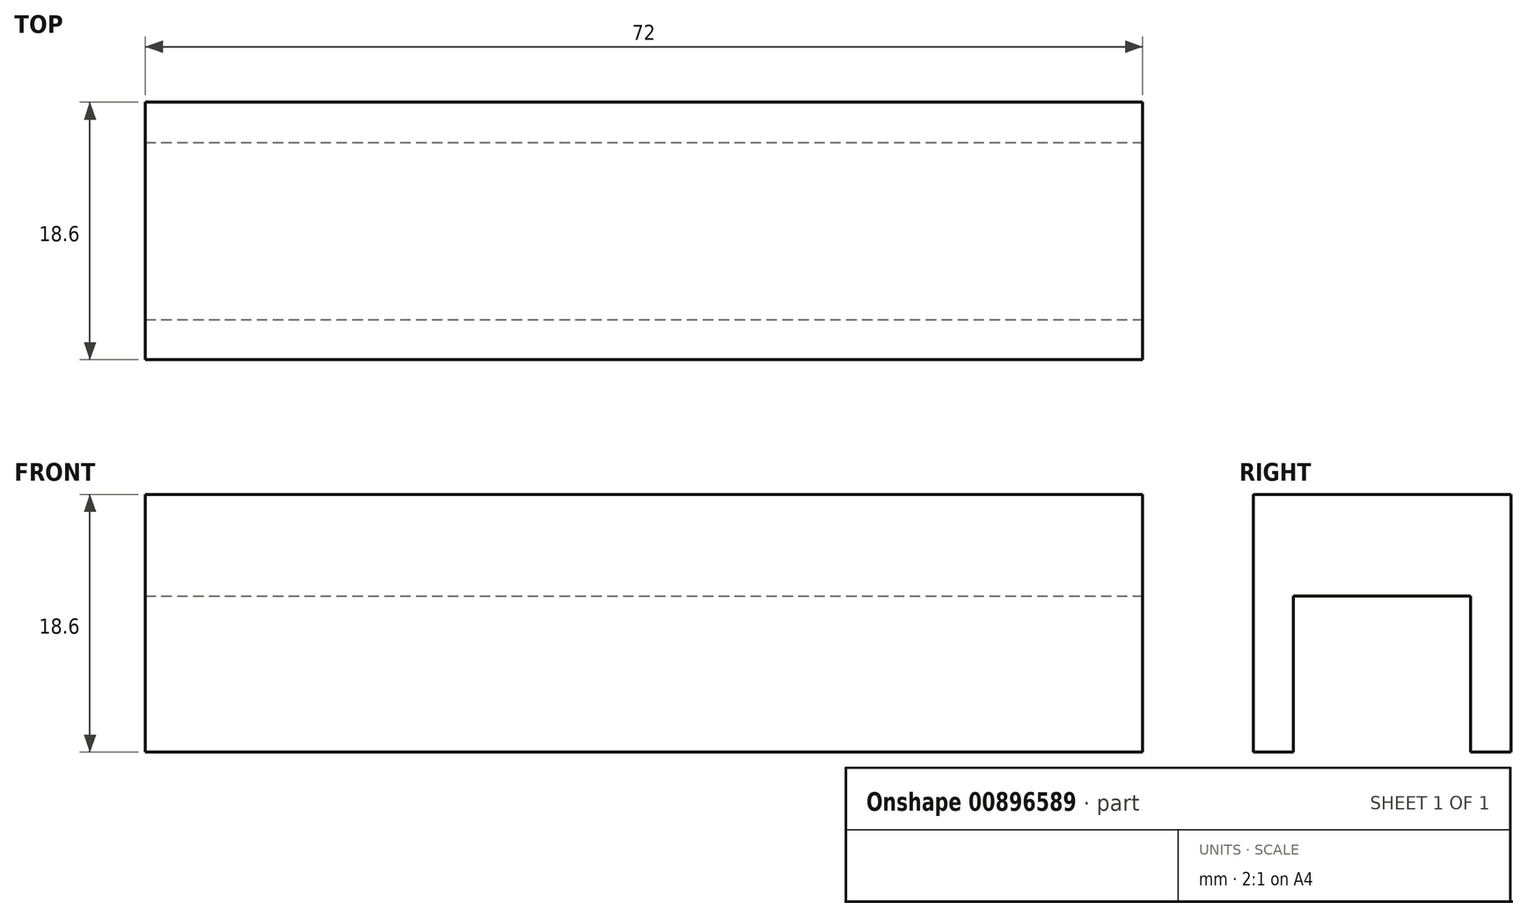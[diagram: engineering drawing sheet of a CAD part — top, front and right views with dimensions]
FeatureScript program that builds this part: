
annotation { "Feature Type Name" : "Feature", "Feature Type Description" : "" }
export const myFeature = defineFeature(function(context is Context, id is Id, definition is map)
    precondition{}
    {
        {
            assignVariable(context, id + "F0", {"name" : "basewall", "anyValue" : 3 * mm});
        }
        {
            assignVariable(context, id + "F1", {"name" : "basedowel", "anyValue" : 12.6 * mm});
        }
        {
            var Q0;
            Q0=qCreatedBy(makeId("Top.planeOp"),FACE);
            var sketch = newSketch(context, id + "F2", { "sketchPlane" : qUnion([Q0])});
            skLineSegment(sketch, "E0.bottom", {"start": v(36, -9.3) * mm, "end": v(-36, -9.3) * mm});
            skLineSegment(sketch, "E0.top", {"start": v(36, 9.3) * mm, "end": v(-36, 9.3) * mm});
            skLineSegment(sketch, "E0.left", {"start": v(36, -9.3) * mm, "end": v(36, 9.3) * mm});
            skLineSegment(sketch, "E0.right", {"start": v(-36, -9.3) * mm, "end": v(-36, 9.3) * mm});
            skPoint(sketch, "E0.middle", {"position": v(0, 0) * mm});
            skSolve(sketch);
        }
        {
            var Q0;
            Q0=makeQuery(id+"F2.imprint","IMPRINT",FACE,{"disambiguationData":[TD([[makeQuery(id+"F2.imprint","IMPRINT",EDGE,{"derivedFrom":sQuery(id+"F2.wireOp",EDGE,"E0.bottom")}),-1.0]])]});
            extrude(context, id + "F3", {"entities" : qUnion([Q0]), "depth" : getVariable(context, 'basedowel') + 2 * getVariable(context, 'basewall'), "offsetDistance" : 25 * mm});
        }
        {
            var Q0;
            Q0=makeQuery(id+"F3.opExtrude","SWEPT_FACE",FACE,{"disambiguationData":[OSD([sQuery(id+"F2.wireOp",EDGE,"E0.left")])]});
            var sketch = newSketch(context, id + "F4", { "sketchPlane" : qUnion([Q0])});
            skLineSegment(sketch, "E1.bottom", {"start": v(6.4, -11.26) * mm, "end": v(-6.4, -11.26) * mm});
            skLineSegment(sketch, "E1.top", {"start": v(6.4, 11.26) * mm, "end": v(-6.4, 11.26) * mm});
            skLineSegment(sketch, "E1.left", {"start": v(6.4, -11.26) * mm, "end": v(6.4, 11.26) * mm});
            skLineSegment(sketch, "E1.right", {"start": v(-6.4, -11.26) * mm, "end": v(-6.4, 11.26) * mm});
            skPoint(sketch, "E1.middle", {"position": v(0, 0) * mm});
            skSolve(sketch);
        }
        {
            var Q0;
            {var subQ0=sQuery(id+"F4.wireOp",EDGE,"E1.top");Q0=makeQuery(id+"F4.imprint","IMPRINT",FACE,{"disambiguationData":[TD([[makeQuery(id+"F4.imprint","IMPRINT",EDGE,{"derivedFrom":subQ0}),1.0]])]});}
            var Q1;
            Q1=makeQuery(id+"F3.opExtrude","SWEPT_FACE",FACE,{"disambiguationData":[OSD([sQuery(id+"F2.wireOp",EDGE,"E0.right")])]});
            var Q2;
            Q2=makeQuery(id+"F3.opExtrude","SWEPT_FACE",FACE,{"disambiguationData":[OSD([sQuery(id+"F2.wireOp",EDGE,"E0.right")])]});
            extrude(context, id + "F5", {"entities" : qUnion([Q0]), "operationType" : NewBodyOperationType.REMOVE, "endBound" : BoundingType.UP_TO_SURFACE, "oppositeDirection" : true, "depth" : 25 * mm, "endBoundEntityFace" : qUnion([Q1]), "offsetDistance" : 25 * mm});
        }
    });
